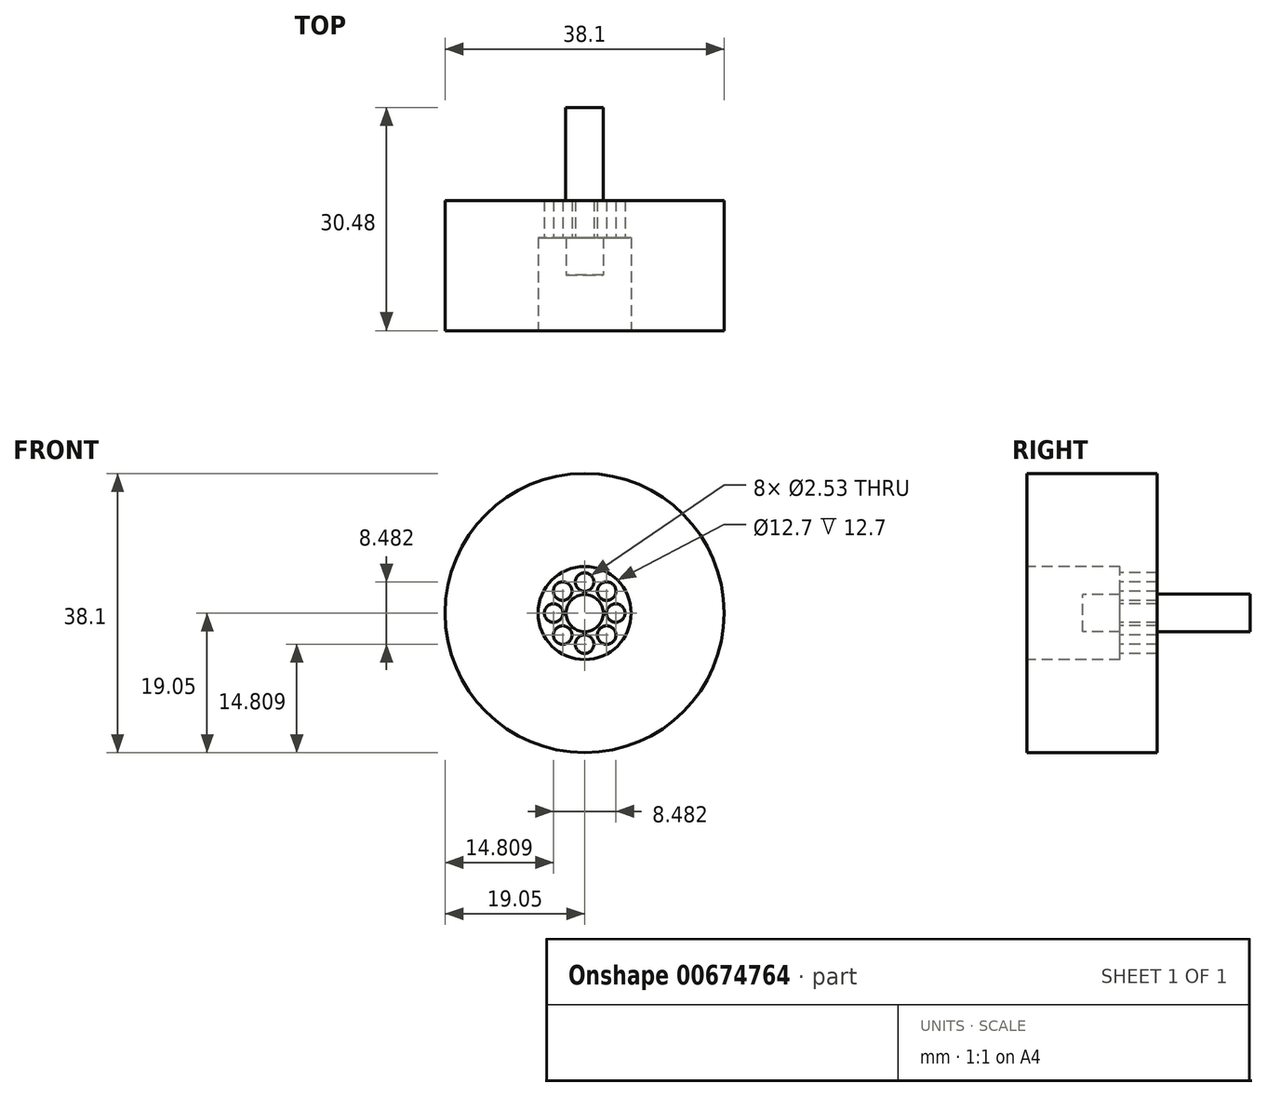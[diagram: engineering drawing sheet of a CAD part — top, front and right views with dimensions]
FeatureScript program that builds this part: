
annotation { "Feature Type Name" : "Feature", "Feature Type Description" : "" }
export const myFeature = defineFeature(function(context is Context, id is Id, definition is map)
    precondition{}
    {
        {
            var Q0;
            Q0=qCreatedBy(makeId("Front.planeOp"),FACE);
            var sketch = newSketch(context, id + "F0", { "sketchPlane" : qUnion([Q0])});
            skCircle(sketch, "E0", {"center": v(0, 0) * mm, "radius": 19.05 * mm});
            skSolve(sketch);
        }
        {
            var Q0;
            Q0 = qSketchRegion(id + "F0", true);
            extrude(context, id + "F1", {"entities" : qUnion([Q0]), "depth" : 17.78 * mm, "offsetDistance" : 25.4 * mm});
        }
        {
            var Q0;
            Q0=makeQuery(id+"F1.opExtrude","CAP_FACE",FACE,{"disambiguationData":[OSD([sQuery(id+"F0.wireOp",EDGE,"E0")])],"isStart":false});
            var sketch = newSketch(context, id + "F2", { "sketchPlane" : qUnion([Q0])});
            skCircle(sketch, "E1", {"center": v(0, 0) * mm, "radius": 2.42 * mm});
            skCircle(sketch, "E2", {"center": v(0, 0) * mm, "radius": 2.54 * mm});
            skSolve(sketch);
        }
        {
            var Q0;
            Q0=makeQuery(id+"F1.opExtrude","CAP_FACE",FACE,{"disambiguationData":[OSD([sQuery(id+"F0.wireOp",EDGE,"E0")])],"isStart":true});
            var sketch = newSketch(context, id + "F3", { "sketchPlane" : qUnion([Q0])});
            skCircle(sketch, "E3", {"center": v(0, 0) * mm, "radius": 2.52 * mm});
            skSolve(sketch);
        }
        {
            var Q0;
            Q0=makeQuery(id+"F2.imprint","IMPRINT",FACE,{"disambiguationData":[TD([[makeQuery(id+"F2.imprint","IMPRINT",EDGE,{"derivedFrom":sQuery(id+"F2.wireOp",EDGE,"E2")}),-1.0]])]});
            var sketch = newSketch(context, id + "F4", { "sketchPlane" : qUnion([Q0])});
            skCircle(sketch, "E4", {"center": v(0, 0) * mm, "radius": 6.35 * mm});
            skSolve(sketch);
        }
        {
            var Q0;
            Q0=makeQuery(id+"F4.imprint","IMPRINT",FACE,{"disambiguationData":[TD([[makeQuery(id+"F4.imprint","IMPRINT",EDGE,{"derivedFrom":sQuery(id+"F4.wireOp",EDGE,"E4")}),1.0]])]});
            extrude(context, id + "F5", {"entities" : qUnion([Q0]), "operationType" : NewBodyOperationType.REMOVE, "oppositeDirection" : true, "depth" : 12.7 * mm, "offsetDistance" : 25.4 * mm});
        }
        {
            var Q0;
            Q0=makeQuery(id+"F2.imprint","IMPRINT",FACE,{"disambiguationData":[TD([[makeQuery(id+"F2.imprint","IMPRINT",EDGE,{"derivedFrom":sQuery(id+"F2.wireOp",EDGE,"E1")}),1.0]])]});
            extrude(context, id + "F6", {"entities" : qUnion([Q0]), "operationType" : NewBodyOperationType.REMOVE, "oppositeDirection" : true, "depth" : 7.62 * mm, "offsetDistance" : 25.4 * mm});
        }
        {
            var Q0;
            Q0=makeQuery(id+"F5.boolean.opBoolean","SPLIT",FACE,{"disambiguationData":[TD([makeQuery(id+"F5.opExtrude","SWEPT_FACE",FACE,{"disambiguationData":[OSD([sQuery(id+"F2.wireOp",EDGE,"E2")])]})])],"derivedFrom":makeQuery(id+"F1.opExtrude","CAP_FACE",FACE,{"disambiguationData":[OSD([sQuery(id+"F0.wireOp",EDGE,"E0")])],"isStart":false})});
            extrude(context, id + "F7", {"entities" : qUnion([Q0]), "operationType" : NewBodyOperationType.REMOVE, "oppositeDirection" : true, "depth" : 7.62 * mm, "offsetDistance" : 25.4 * mm});
        }
        {
            var Q0;
            Q0=makeQuery(id+"F5.boolean.opBoolean","COPY",FACE,{"derivedFrom":makeQuery(id+"F5.opExtrude","CAP_FACE",FACE,{"disambiguationData":[OSD([sQuery(id+"F2.wireOp",EDGE,"E2"),sQuery(id+"F4.wireOp",EDGE,"E4")])],"isStart":false})});
            var sketch = newSketch(context, id + "F8", { "sketchPlane" : qUnion([Q0])});
            skCircle(sketch, "E5", {"center": v(0, 4.24) * mm, "radius": 1.27 * mm});
            skCircle(sketch, "E6.1.0", {"center": v(-3, 3) * mm, "radius": 1.27 * mm});
            skCircle(sketch, "E6.2.0", {"center": v(-4.24, 0) * mm, "radius": 1.27 * mm});
            skCircle(sketch, "E6.3.0", {"center": v(-3, -3) * mm, "radius": 1.27 * mm});
            skCircle(sketch, "E6.4.0", {"center": v(0, -4.24) * mm, "radius": 1.27 * mm});
            skCircle(sketch, "E6.5.0", {"center": v(3, -3) * mm, "radius": 1.27 * mm});
            skCircle(sketch, "E6.6.0", {"center": v(4.24, 0) * mm, "radius": 1.27 * mm});
            skCircle(sketch, "E6.7.0", {"center": v(3, 3) * mm, "radius": 1.27 * mm});
            skPoint(sketch, "E6.center", {"position": v(0, 0) * mm});
            skSolve(sketch);
        }
        {
            var Q0;
            Q0=makeQuery(id+"F8.imprint","IMPRINT",FACE,{"disambiguationData":[TD([[makeQuery(id+"F8.imprint","IMPRINT",EDGE,{"derivedFrom":sQuery(id+"F8.wireOp",EDGE,"E6.2.0")}),1.0]])]});
            var Q1;
            Q1=makeQuery(id+"F8.imprint","IMPRINT",FACE,{"disambiguationData":[TD([[makeQuery(id+"F8.imprint","IMPRINT",EDGE,{"derivedFrom":sQuery(id+"F8.wireOp",EDGE,"E6.1.0")}),1.0]])]});
            var Q2;
            Q2=makeQuery(id+"F8.imprint","IMPRINT",FACE,{"disambiguationData":[TD([[makeQuery(id+"F8.imprint","IMPRINT",EDGE,{"derivedFrom":sQuery(id+"F8.wireOp",EDGE,"E5")}),1.0]])]});
            var Q3;
            Q3=makeQuery(id+"F8.imprint","IMPRINT",FACE,{"disambiguationData":[TD([[makeQuery(id+"F8.imprint","IMPRINT",EDGE,{"derivedFrom":sQuery(id+"F8.wireOp",EDGE,"E6.7.0")}),1.0]])]});
            var Q4;
            Q4=makeQuery(id+"F8.imprint","IMPRINT",FACE,{"disambiguationData":[TD([[makeQuery(id+"F8.imprint","IMPRINT",EDGE,{"derivedFrom":sQuery(id+"F8.wireOp",EDGE,"E6.6.0")}),1.0]])]});
            var Q5;
            Q5=makeQuery(id+"F8.imprint","IMPRINT",FACE,{"disambiguationData":[TD([[makeQuery(id+"F8.imprint","IMPRINT",EDGE,{"derivedFrom":sQuery(id+"F8.wireOp",EDGE,"E6.5.0")}),1.0]])]});
            var Q6;
            Q6=makeQuery(id+"F8.imprint","IMPRINT",FACE,{"disambiguationData":[TD([[makeQuery(id+"F8.imprint","IMPRINT",EDGE,{"derivedFrom":sQuery(id+"F8.wireOp",EDGE,"E6.4.0")}),1.0]])]});
            var Q7;
            Q7=makeQuery(id+"F8.imprint","IMPRINT",FACE,{"disambiguationData":[TD([[makeQuery(id+"F8.imprint","IMPRINT",EDGE,{"derivedFrom":sQuery(id+"F8.wireOp",EDGE,"E6.3.0")}),1.0]])]});
            extrude(context, id + "F9", {"entities" : qUnion([Q0, Q1, Q2, Q3, Q4, Q5, Q6, Q7]), "operationType" : NewBodyOperationType.REMOVE, "oppositeDirection" : true, "depth" : 2.54 * mm, "offsetDistance" : 25.4 * mm});
        }
        {
            var Q0;
            Q0=makeQuery(id+"F9.boolean.opBoolean","COPY",FACE,{"derivedFrom":makeQuery(id+"F9.opExtrude","CAP_FACE",FACE,{"disambiguationData":[OSD([sQuery(id+"F8.wireOp",EDGE,"E6.1.0")])],"isStart":false})});
            var Q1;
            Q1=makeQuery(id+"F9.boolean.opBoolean","COPY",FACE,{"derivedFrom":makeQuery(id+"F9.opExtrude","CAP_FACE",FACE,{"disambiguationData":[OSD([sQuery(id+"F8.wireOp",EDGE,"E6.2.0")])],"isStart":false})});
            var Q2;
            Q2=makeQuery(id+"F9.boolean.opBoolean","COPY",FACE,{"derivedFrom":makeQuery(id+"F9.opExtrude","CAP_FACE",FACE,{"disambiguationData":[OSD([sQuery(id+"F8.wireOp",EDGE,"E6.3.0")])],"isStart":false})});
            var Q3;
            Q3=makeQuery(id+"F9.boolean.opBoolean","COPY",FACE,{"derivedFrom":makeQuery(id+"F9.opExtrude","CAP_FACE",FACE,{"disambiguationData":[OSD([sQuery(id+"F8.wireOp",EDGE,"E6.4.0")])],"isStart":false})});
            var Q4;
            Q4=makeQuery(id+"F9.boolean.opBoolean","COPY",FACE,{"derivedFrom":makeQuery(id+"F9.opExtrude","CAP_FACE",FACE,{"disambiguationData":[OSD([sQuery(id+"F8.wireOp",EDGE,"E6.5.0")])],"isStart":false})});
            var Q5;
            Q5=makeQuery(id+"F9.boolean.opBoolean","COPY",FACE,{"derivedFrom":makeQuery(id+"F9.opExtrude","CAP_FACE",FACE,{"disambiguationData":[OSD([sQuery(id+"F8.wireOp",EDGE,"E6.6.0")])],"isStart":false})});
            var Q6;
            Q6=makeQuery(id+"F9.boolean.opBoolean","COPY",FACE,{"derivedFrom":makeQuery(id+"F9.opExtrude","CAP_FACE",FACE,{"disambiguationData":[OSD([sQuery(id+"F8.wireOp",EDGE,"E6.7.0")])],"isStart":false})});
            var Q7;
            Q7=makeQuery(id+"F9.boolean.opBoolean","COPY",FACE,{"derivedFrom":makeQuery(id+"F9.opExtrude","CAP_FACE",FACE,{"disambiguationData":[OSD([sQuery(id+"F8.wireOp",EDGE,"E5")])],"isStart":false})});
            extrude(context, id + "F10", {"entities" : qUnion([Q0, Q1, Q2, Q3, Q4, Q5, Q6, Q7]), "operationType" : NewBodyOperationType.REMOVE, "oppositeDirection" : true, "depth" : 25.4 * mm, "offsetDistance" : 25.4 * mm});
        }
        {
            var Q0;
            Q0=makeQuery(id+"F3.imprint","IMPRINT",FACE,{"disambiguationData":[TD([[makeQuery(id+"F3.imprint","IMPRINT",EDGE,{"derivedFrom":sQuery(id+"F3.wireOp",EDGE,"E3")}),1.0]])]});
            var sketch = newSketch(context, id + "F11", { "sketchPlane" : qUnion([Q0])});
            skCircle(sketch, "E7", {"center": v(0, 0) * mm, "radius": 2.57 * mm});
            skSolve(sketch);
        }
        {
            var Q0;
            Q0 = qSketchRegion(id + "F11", true);
            var Q1;
            Q1=makeQuery(id+"F3.imprint","IMPRINT",FACE,{"disambiguationData":[TD([[makeQuery(id+"F3.imprint","IMPRINT",EDGE,{"derivedFrom":sQuery(id+"F3.wireOp",EDGE,"E3")}),1.0]])]});
            extrude(context, id + "F12", {"entities" : qUnion([Q0, Q1]), "operationType" : NewBodyOperationType.ADD, "depth" : 12.7 * mm, "offsetDistance" : 25.4 * mm});
        }
    });
